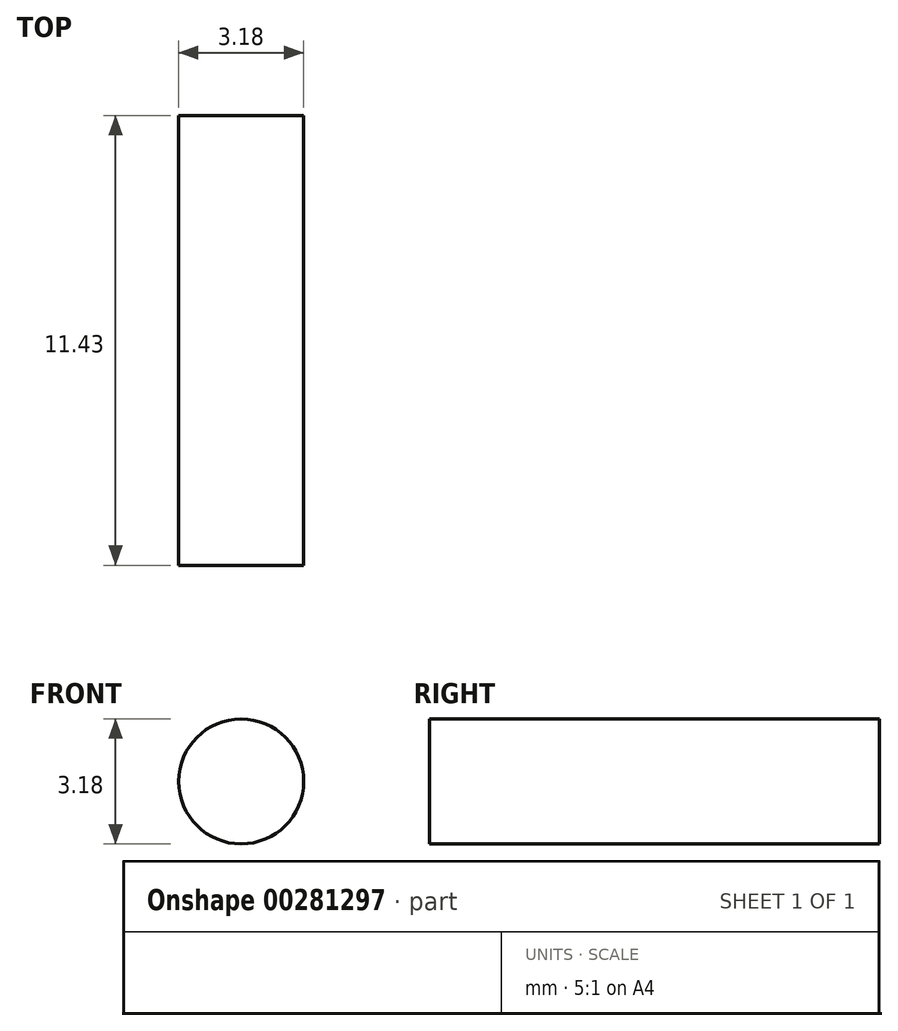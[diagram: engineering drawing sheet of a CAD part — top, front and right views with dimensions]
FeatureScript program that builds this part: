
annotation { "Feature Type Name" : "Feature", "Feature Type Description" : "" }
export const myFeature = defineFeature(function(context is Context, id is Id, definition is map)
    precondition{}
    {
        {
            var Q0;
            Q0=qCreatedBy(makeId("Front.planeOp"),FACE);
            var sketch = newSketch(context, id + "F0", { "sketchPlane" : qUnion([Q0])});
            skCircle(sketch, "E0", {"center": v(0, 0) * mm, "radius": 1.59 * mm});
            skSolve(sketch);
        }
        {
            var Q0;
            Q0 = qSketchRegion(id + "F0", true);
            extrude(context, id + "F1", {"entities" : qUnion([Q0]), "depth" : 11.43 * mm});
        }
    });
